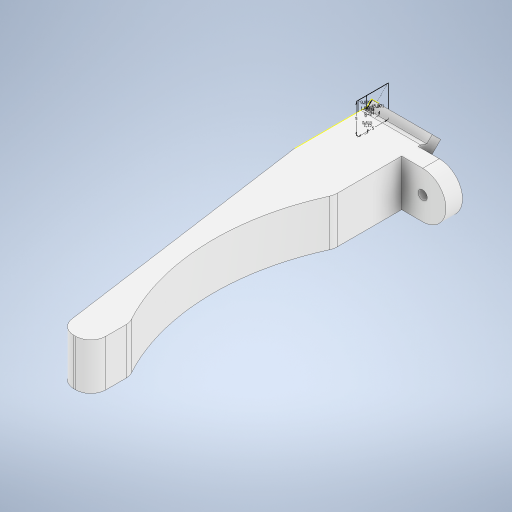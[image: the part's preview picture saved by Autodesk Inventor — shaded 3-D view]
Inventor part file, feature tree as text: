
AUTODESK INVENTOR PART (.ipt)
format: ipt  version: 2024 (Build 280153000, 153)  size: 702,976 bytes
history: native  units: in
note: dims shown in document units (in); Inventor stores cm internally (conversion verified against a paired STEP export)
features: extrude x4, sketch x2, other x1, plane x1, mirror x1, projected_geometry x1, fillet x1
ambient origin geometry x8: Origin, YZ Plane, XZ Plane, XY Plane, X Axis, Y Axis, Z Axis, Center Point
bodies: Solid1 (feature_tree)
feature tree (11):
  other  "Plane1"
  sketch  "Sketch1"  dims[d10=0.0787in d11=0.0787in]
  extrude  "Extrusion1"  Depth=0.0787in
  extrude  "Extrusion2"  Depth=0.3937in
  plane  "Work Plane2"
  extrude  "Extrusion3"  TaperAngle=0.0deg  [1 undecoded]
  extrude  "Extrusion4"  TaperAngle=0.0deg  [1 undecoded]
  mirror  "Mirror1"
  projected_geometry  "Projected Loop1"
  sketch  "Sketch2"  dims[d12=45.0deg d13=0.0414in d14=0.0in d15=0.0in d16=0.035in d17=0.0461in d18=0.0242in d19=0.0108in d20=0.035in d21=0.1969in d22=0.1969in d23=0.0134in d24=0.0423in d25=0.0in d26=0.0in d27=0.3937in d28=0.0in d29=0.0846in d30=0.0846in d31=0.3937in d32=0.0in d33=0.0394in d34=0.0394in d35=0.0in d36=0.0in]
  fillet  "Fillet1"  Radius=0.035in
note: 2 required parameter values undecoded (feature->parameter linkage not recoverable at this tier; creation-order binding heuristic only, values carry confidence <= 0.55)
